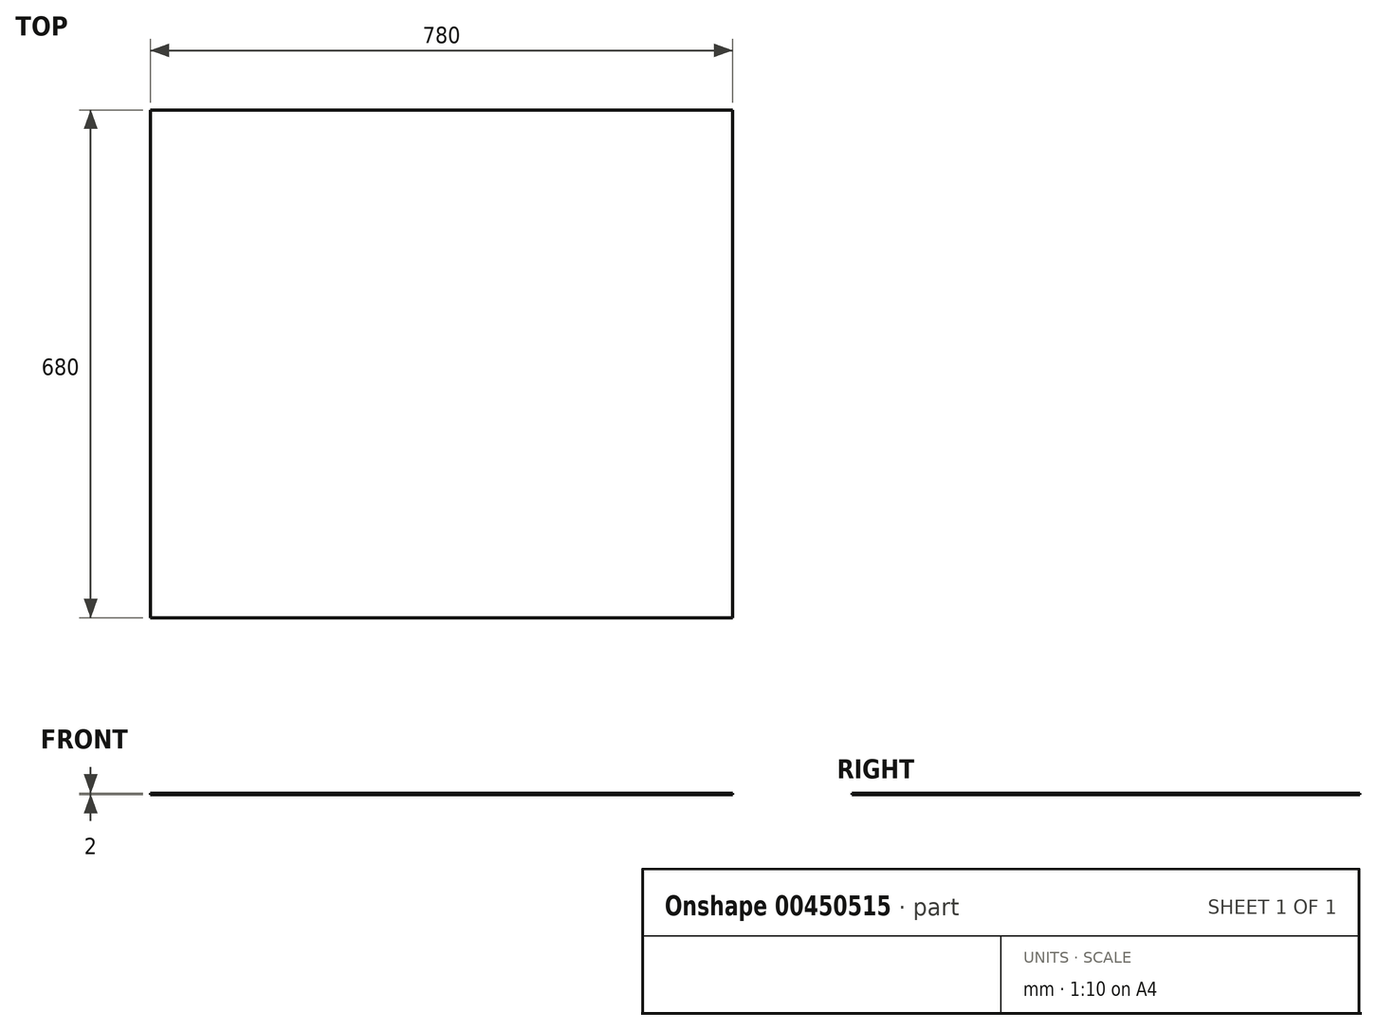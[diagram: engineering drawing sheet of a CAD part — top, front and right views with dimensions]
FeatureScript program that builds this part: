
annotation { "Feature Type Name" : "Feature", "Feature Type Description" : "" }
export const myFeature = defineFeature(function(context is Context, id is Id, definition is map)
    precondition{}
    {
        {
            var Q0;
            Q0=qCreatedBy(makeId("Top.planeOp"),FACE);
            var sketch = newSketch(context, id + "F0", { "sketchPlane" : qUnion([Q0])});
            skLineSegment(sketch, "E0.bottom", {"start": v(-390, 340) * mm, "end": v(390, 340) * mm});
            skLineSegment(sketch, "E0.top", {"start": v(-390, -340) * mm, "end": v(390, -340) * mm});
            skLineSegment(sketch, "E0.left", {"start": v(-390, 340) * mm, "end": v(-390, -340) * mm});
            skLineSegment(sketch, "E0.right", {"start": v(390, 340) * mm, "end": v(390, -340) * mm});
            skPoint(sketch, "E0.middle", {"position": v(0, 0) * mm});
            skSolve(sketch);
        }
        {
            var Q0;
            Q0=makeQuery(id+"F0.imprint","IMPRINT",FACE,{"disambiguationData":[TD([[makeQuery(id+"F0.imprint","IMPRINT",EDGE,{"derivedFrom":sQuery(id+"F0.wireOp",EDGE,"E0.bottom")}),-1.0]])]});
            extrude(context, id + "F1", {"entities" : qUnion([Q0]), "endBound" : BoundingType.SYMMETRIC, "depth" : 2 * mm});
        }
    });
